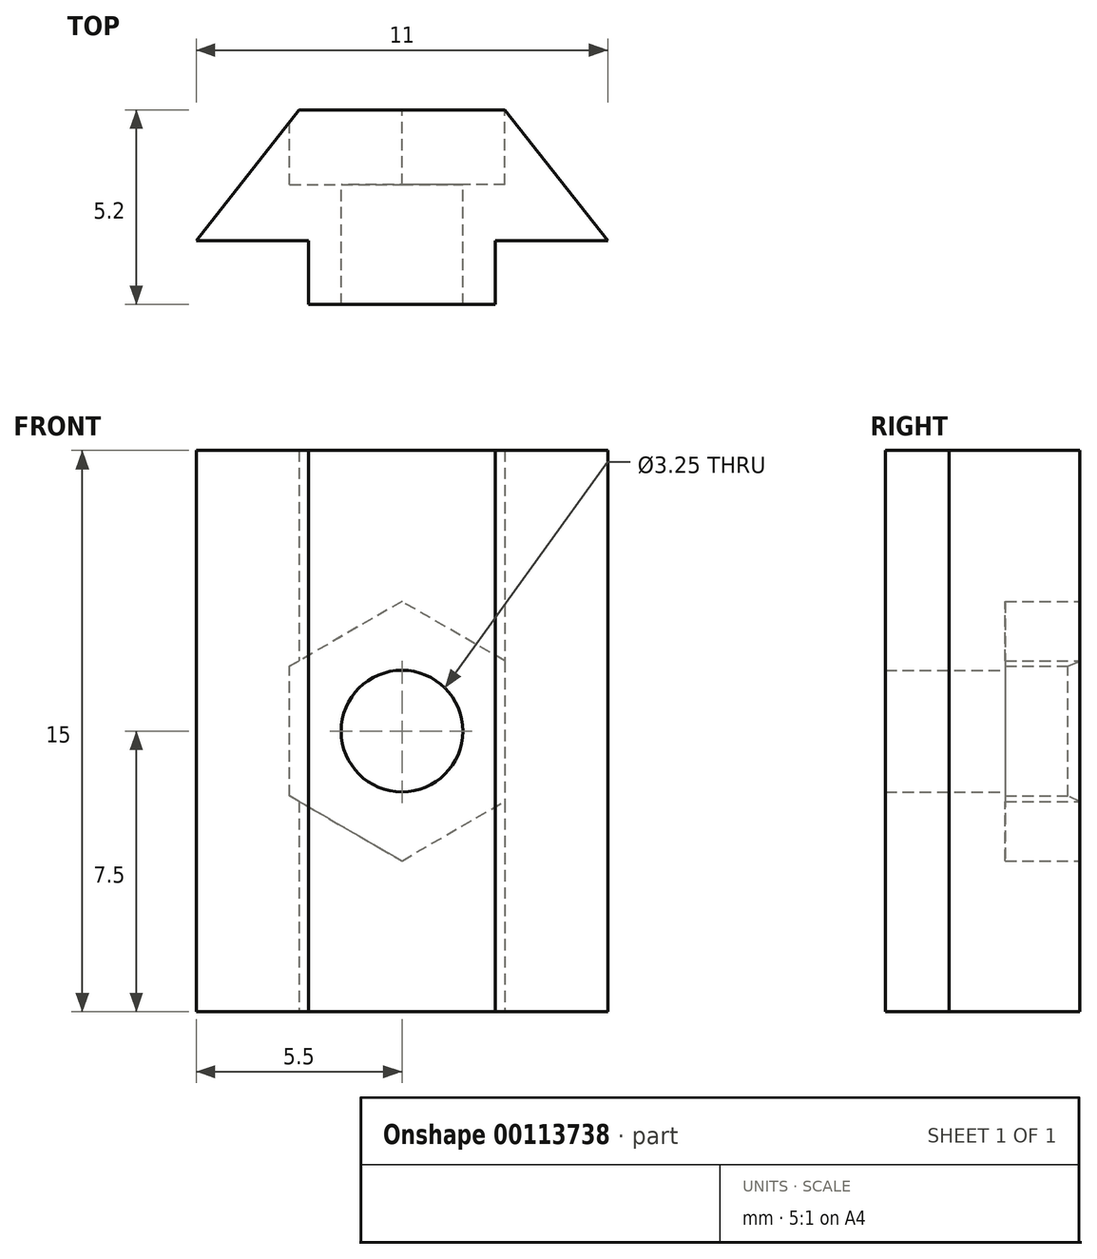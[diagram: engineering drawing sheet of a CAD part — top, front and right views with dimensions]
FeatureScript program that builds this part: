
annotation { "Feature Type Name" : "Feature", "Feature Type Description" : "" }
export const myFeature = defineFeature(function(context is Context, id is Id, definition is map)
    precondition{}
    {
        {
            var Q0;
            Q0=qCreatedBy(makeId("Top.planeOp"),FACE);
            var sketch = newSketch(context, id + "F0", { "sketchPlane" : qUnion([Q0])});
            skLineSegment(sketch, "E0", {"start": v(12.14, 7.45) * mm, "end": v(12.14, 3.95) * mm, "construction": true});
            skLineSegment(sketch, "E1", {"start": v(12.14, 7.45) * mm, "end": v(9.39, 7.45) * mm});
            skLineSegment(sketch, "E2", {"start": v(9.39, 7.45) * mm, "end": v(6.64, 3.95) * mm});
            skLineSegment(sketch, "E3", {"start": v(6.64, 3.95) * mm, "end": v(12.14, 3.95) * mm});
            skLineSegment(sketch, "E4.MirrorCS", {"start": v(14.89, 7.45) * mm, "end": v(17.64, 3.95) * mm});
            skLineSegment(sketch, "E5.MirrorCS", {"start": v(12.14, 7.45) * mm, "end": v(14.89, 7.45) * mm});
            skLineSegment(sketch, "E6.MirrorCS", {"start": v(17.64, 3.95) * mm, "end": v(12.14, 3.95) * mm});
            skSolve(sketch);
        }
        {
            var Q0;
            Q0=makeQuery(id+"F0.imprint","IMPRINT",FACE,{"disambiguationData":[TD([[makeQuery(id+"F0.imprint","IMPRINT",EDGE,{"derivedFrom":sQuery(id+"F0.wireOp",EDGE,"E1")}),1.0]])]});
            extrude(context, id + "F1", {"entities" : qUnion([Q0]), "depth" : 15 * mm});
        }
        {
            var Q0;
            Q0=makeQuery(id+"F1.opExtrude","SWEPT_FACE",FACE,{"disambiguationData":[OSD([sQuery(id+"F0.wireOp",EDGE,"E1"),sQuery(id+"F0.wireOp",EDGE,"E5.MirrorCS")])]});
            var sketch = newSketch(context, id + "F2", { "sketchPlane" : qUnion([Q0])});
            skCircle(sketch, "E7.cCircle", {"center": v(-12.14, 7.5) * mm, "radius": 3 * mm, "construction": true});
            skPoint(sketch, "E7.cCircle.centerSnap0", {"position": v(-12.14, 15) * mm});
            skPoint(sketch, "E7.cCircle.centerSnap1", {"position": v(-9.39, 7.5) * mm});
            skLineSegment(sketch, "E7.0", {"start": v(-9.14, 9.23) * mm, "end": v(-9.14, 5.77) * mm});
            skLineSegment(sketch, "E7.1", {"start": v(-9.14, 5.77) * mm, "end": v(-12.14, 4.04) * mm});
            skLineSegment(sketch, "E7.2", {"start": v(-12.14, 4.04) * mm, "end": v(-15.14, 5.77) * mm});
            skLineSegment(sketch, "E7.3", {"start": v(-15.14, 5.77) * mm, "end": v(-15.14, 9.23) * mm});
            skLineSegment(sketch, "E7.4", {"start": v(-15.14, 9.23) * mm, "end": v(-12.14, 10.96) * mm});
            skLineSegment(sketch, "E7.5", {"start": v(-12.14, 10.96) * mm, "end": v(-9.14, 9.23) * mm});
            skPoint(sketch, "E7.0.midPoint", {"position": v(-9.14, 7.5) * mm});
            skCircle(sketch, "E8", {"center": v(-12.14, 7.5) * mm, "radius": 1.63 * mm});
            skSolve(sketch);
        }
        {
            var Q0;
            Q0=makeQuery(id+"F2.imprint","IMPRINT",FACE,{"disambiguationData":[TD([[makeQuery(id+"F2.imprint","IMPRINT",EDGE,{"derivedFrom":sQuery(id+"F2.wireOp",EDGE,"E8")}),1.0]])]});
            extrude(context, id + "F3", {"entities" : qUnion([Q0]), "operationType" : NewBodyOperationType.REMOVE, "oppositeDirection" : true, "depth" : 25 * mm});
        }
        {
            var Q0;
            Q0=makeQuery(id+"F2.imprint","IMPRINT",FACE,{"disambiguationData":[TD([[makeQuery(id+"F2.imprint","IMPRINT",EDGE,{"derivedFrom":sQuery(id+"F2.wireOp",EDGE,"E7.0")}),-1.0]])]});
            var Q1;
            Q1=makeQuery(id+"F2.imprint","IMPRINT",FACE,{"disambiguationData":[TD([[makeQuery(id+"F2.imprint","IMPRINT",EDGE,{"derivedFrom":sQuery(id+"F2.wireOp",EDGE,"E8")}),-1.0]])]});
            extrude(context, id + "F4", {"entities" : qUnion([Q0, Q1]), "operationType" : NewBodyOperationType.REMOVE, "oppositeDirection" : true, "depth" : 2 * mm});
        }
        {
            var Q0;
            Q0=makeQuery(id+"F1.opExtrude","SWEPT_FACE",FACE,{"disambiguationData":[OSD([sQuery(id+"F0.wireOp",EDGE,"E3"),sQuery(id+"F0.wireOp",EDGE,"E6.MirrorCS")])]});
            var sketch = newSketch(context, id + "F5", { "sketchPlane" : qUnion([Q0])});
            skLineSegment(sketch, "E9.bottom", {"start": v(9.64, 15) * mm, "end": v(14.64, 15) * mm});
            skLineSegment(sketch, "E9.top", {"start": v(9.64, 0) * mm, "end": v(14.64, 0) * mm});
            skLineSegment(sketch, "E9.left", {"start": v(9.64, 15) * mm, "end": v(9.64, 0) * mm});
            skLineSegment(sketch, "E9.right", {"start": v(14.64, 15) * mm, "end": v(14.64, 0) * mm});
            skLineSegment(sketch, "E10", {"start": v(12.14, 15) * mm, "end": v(12.14, 0) * mm, "construction": true});
            skSolve(sketch);
        }
        {
            var Q0;
            Q0=makeQuery(id+"F5.imprint","IMPRINT",FACE,{"disambiguationData":[TD([[makeQuery(id+"F5.imprint","IMPRINT",EDGE,{"derivedFrom":sQuery(id+"F5.wireOp",EDGE,"E9.bottom")}),-1.0]])]});
            extrude(context, id + "F6", {"entities" : qUnion([Q0]), "operationType" : NewBodyOperationType.ADD, "depth" : 1.7 * mm});
        }
    });
